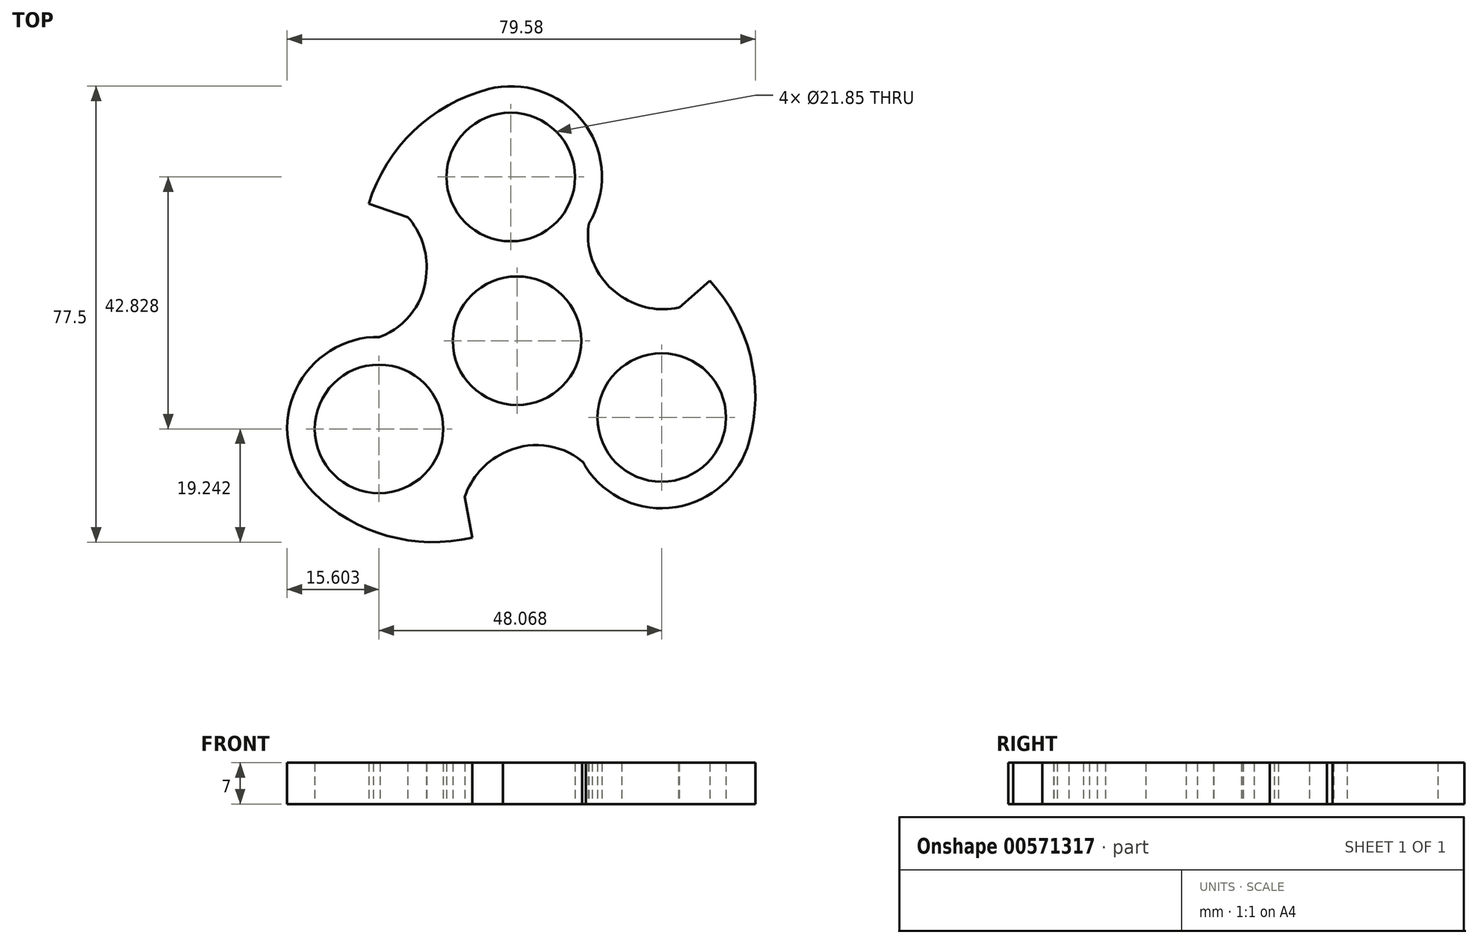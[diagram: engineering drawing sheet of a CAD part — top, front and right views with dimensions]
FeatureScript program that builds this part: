
annotation { "Feature Type Name" : "Feature", "Feature Type Description" : "" }
export const myFeature = defineFeature(function(context is Context, id is Id, definition is map)
    precondition{}
    {
        {
            var Q0;
            Q0=qCreatedBy(makeId("Top.planeOp"),FACE);
            var sketch = newSketch(context, id + "F0", { "sketchPlane" : qUnion([Q0])});
            skCircle(sketch, "E0", {"center": v(0, 0) * mm, "radius": 10.93 * mm});
            skCircle(sketch, "E1", {"center": v(-1.07, 27.83) * mm, "radius": 10.93 * mm});
            skCircle(sketch, "E2.1.0", {"center": v(-23.47, -15) * mm, "radius": 10.93 * mm});
            skCircle(sketch, "E2.2.0", {"center": v(24.6, -13.05) * mm, "radius": 10.93 * mm});
            skPoint(sketch, "E3.start.orphan", {"position": v(0, 43.22) * mm});
            skLineSegment(sketch, "E4.2.0", {"start": v(-18.58, 21) * mm, "end": v(-25.2, 23.3) * mm});
            skArc(sketch, "E5.1.3", {"start": v(-23.31, 0.64) * mm, "mid": v(-17.7, 4.96) * mm, "end": v(-15.39, 11.67) * mm});
            skArc(sketch, "E5.2.0", {"start": v(12.77, 20.87) * mm, "mid": v(11.01, 37.51) * mm, "end": v(-4.88, 42.76) * mm});
            skArc(sketch, "E5.2.1", {"start": v(-4.88, 42.76) * mm, "mid": v(-17.57, 35.67) * mm, "end": v(-25.2, 23.3) * mm});
            skArc(sketch, "E6", {"start": v(-15.39, 11.67) * mm, "mid": v(-16.05, 16.66) * mm, "end": v(-18.58, 21) * mm});
            skPoint(sketch, "E7.orphan", {"position": v(12.21, 19.87) * mm});
            skPoint(sketch, "E8.2.0.end.orphan", {"position": v(32.77, 10.17) * mm});
            skPoint(sketch, "E9.orphan", {"position": v(11.1, -20.51) * mm});
            skPoint(sketch, "E10.trimOffspring.end.orphan", {"position": v(27.48, 5.59) * mm});
            skArc(sketch, "E11.1.0", {"start": v(11.1, -20.51) * mm, "mid": v(4.55, -17.8) * mm, "end": v(-2.41, -19.16) * mm});
            skArc(sketch, "E11.1.1", {"start": v(-2.41, -19.16) * mm, "mid": v(-6.36, -22.19) * mm, "end": v(-8.87, -26.5) * mm});
            skLineSegment(sketch, "E11.1.2", {"start": v(-8.87, -26.6) * mm, "end": v(-7.57, -33.47) * mm});
            skArc(sketch, "E11.1.3", {"start": v(-34.6, -25.8) * mm, "mid": v(-22.08, -33.15) * mm, "end": v(-7.57, -33.47) * mm});
            skArc(sketch, "E11.1.4", {"start": v(-24.46, 0.62) * mm, "mid": v(-38.04, -9.33) * mm, "end": v(-34.6, -25.8) * mm});
            skArc(sketch, "E11.2.0", {"start": v(12.21, 19.87) * mm, "mid": v(13.14, 12.84) * mm, "end": v(17.8, 7.5) * mm});
            skArc(sketch, "E11.2.1", {"start": v(17.8, 7.5) * mm, "mid": v(22.45, 5.58) * mm, "end": v(27.47, 5.6) * mm});
            skLineSegment(sketch, "E11.2.2", {"start": v(27.55, 5.65) * mm, "end": v(32.77, 10.17) * mm});
            skArc(sketch, "E11.2.3", {"start": v(39.47, -17.15) * mm, "mid": v(39.68, -2.62) * mm, "end": v(32.77, 10.17) * mm});
            skArc(sketch, "E11.2.4", {"start": v(11.69, -21.5) * mm, "mid": v(26.98, -28.3) * mm, "end": v(39.47, -17.15) * mm});
            skArc(sketch, "E12", {"start": v(11.69, -21.5) * mm, "mid": v(11.44, -20.97) * mm, "end": v(11.1, -20.51) * mm});
            skArc(sketch, "E13", {"start": v(-24.46, 0.62) * mm, "mid": v(-23.88, 0.61) * mm, "end": v(-23.31, 0.64) * mm});
            skArc(sketch, "E14", {"start": v(12.77, 20.87) * mm, "mid": v(12.46, 20.38) * mm, "end": v(12.21, 19.87) * mm});
            skLineSegment(sketch, "E15", {"start": v(-8.87, -26.5) * mm, "end": v(-8.87, -26.6) * mm});
            skPoint(sketch, "E16.orphan", {"position": v(-8.9, -26.47) * mm});
            skLineSegment(sketch, "E17", {"start": v(27.47, 5.6) * mm, "end": v(27.55, 5.65) * mm});
            skSolve(sketch);
        }
        {
            var Q0;
            Q0=qSketchRegion(id+"F0",true);
            extrude(context, id + "F1", {"entities" : qUnion([Q0]), "depth" : 7 * mm, "offsetDistance" : 25 * mm});
        }
    });
